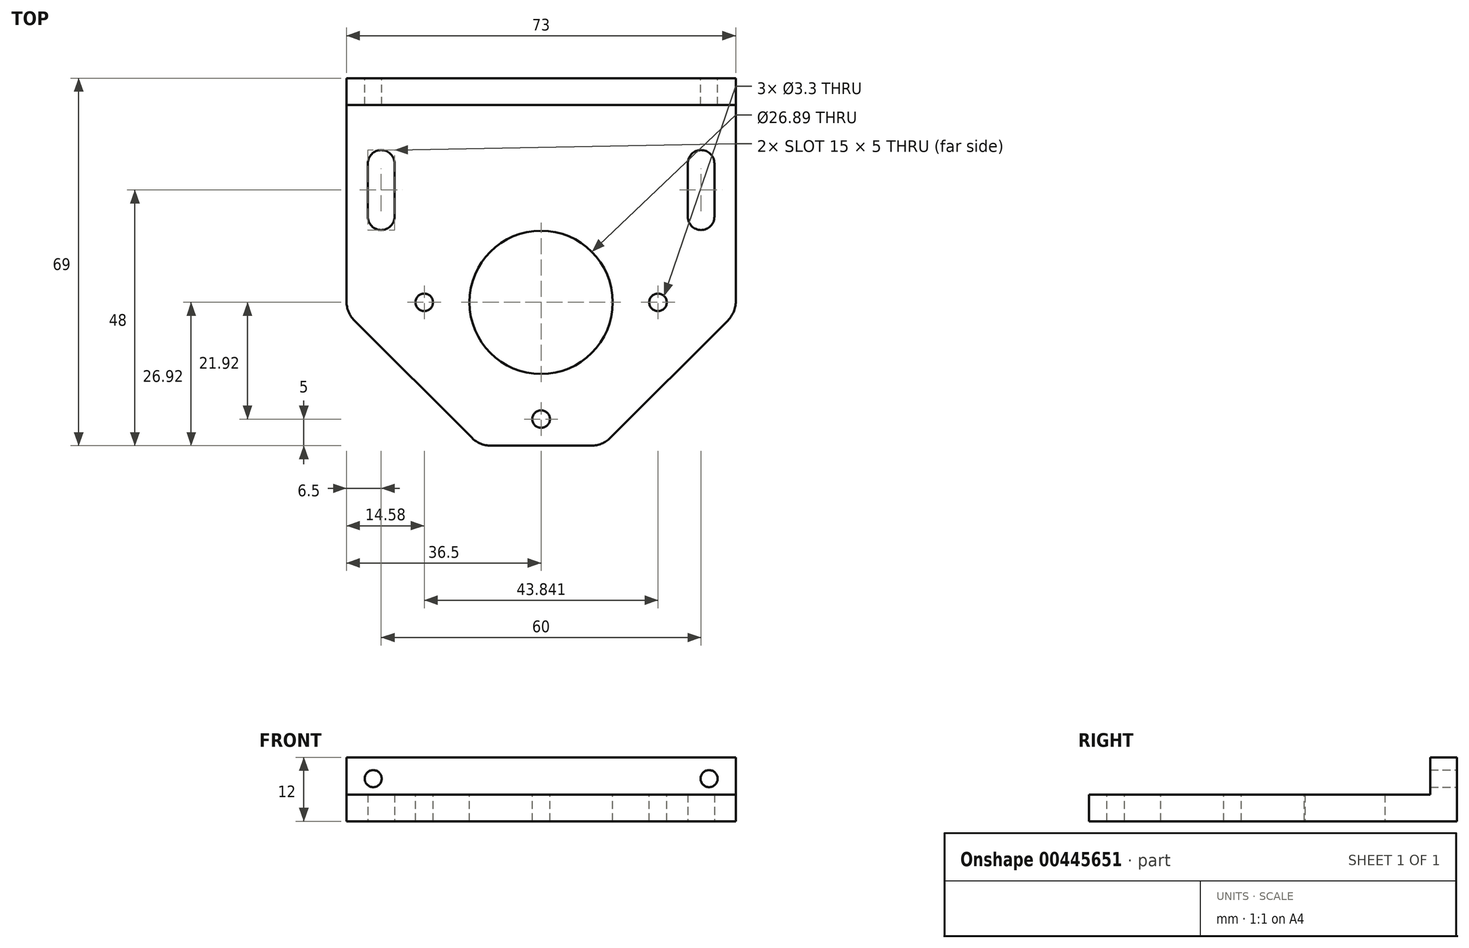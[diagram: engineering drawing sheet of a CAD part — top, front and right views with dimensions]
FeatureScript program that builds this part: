
annotation { "Feature Type Name" : "Feature", "Feature Type Description" : "" }
export const myFeature = defineFeature(function(context is Context, id is Id, definition is map)
    precondition{}
    {
        {
            var Q0;
            Q0=qCreatedBy(makeId("Top.planeOp"),FACE);
            var sketch = newSketch(context, id + "F0", { "sketchPlane" : qUnion([Q0])});
            skLineSegment(sketch, "E0.bottom", {"start": v(-36.5, -29.5) * mm, "end": v(36.5, -29.5) * mm});
            skLineSegment(sketch, "E0.top", {"start": v(-36.5, 29.5) * mm, "end": v(36.5, 29.5) * mm});
            skLineSegment(sketch, "E0.left", {"start": v(-36.5, -29.5) * mm, "end": v(-36.5, 29.5) * mm});
            skLineSegment(sketch, "E0.right", {"start": v(36.5, -29.5) * mm, "end": v(36.5, 29.5) * mm});
            skPoint(sketch, "E0.middle", {"position": v(0, 0) * mm});
            skLineSegment(sketch, "E1", {"start": v(-30, 23.5) * mm, "end": v(-30, 13.5) * mm});
            skLineSegment(sketch, "E2.1.0.0", {"start": v(30, 23.5) * mm, "end": v(30, 13.5) * mm});
            skLineSegment(sketch, "E2.direction1", {"start": v(-30, 13.5) * mm, "end": v(30, 13.5) * mm, "construction": true});
            skArc(sketch, "E3.0.startCap", {"start": v(-32.5, 23.5) * mm, "mid": v(-30, 26) * mm, "end": v(-27.5, 23.5) * mm});
            skArc(sketch, "E3.0.endCap", {"start": v(-27.5, 13.5) * mm, "mid": v(-30, 11) * mm, "end": v(-32.5, 13.5) * mm});
            skLineSegment(sketch, "E3.0.left", {"start": v(-27.5, 23.5) * mm, "end": v(-27.5, 13.5) * mm});
            skLineSegment(sketch, "E3.0.right", {"start": v(-32.5, 23.5) * mm, "end": v(-32.5, 13.5) * mm});
            skArc(sketch, "E3.1.startCap", {"start": v(27.5, 23.5) * mm, "mid": v(30, 26) * mm, "end": v(32.5, 23.5) * mm});
            skArc(sketch, "E3.1.endCap", {"start": v(32.5, 13.5) * mm, "mid": v(30, 11) * mm, "end": v(27.5, 13.5) * mm});
            skLineSegment(sketch, "E3.1.left", {"start": v(32.5, 23.5) * mm, "end": v(32.5, 13.5) * mm});
            skLineSegment(sketch, "E3.1.right", {"start": v(27.5, 23.5) * mm, "end": v(27.5, 13.5) * mm});
            skSolve(sketch);
        }
        {
            var Q0;
            Q0=qSketchRegion(id+"F0",true);
            extrude(context, id + "F1", {"entities" : qUnion([Q0]), "depth" : 5 * mm});
        }
        {
            var Q0;
            Q0=makeQuery(id+"F1.opExtrude","SWEPT_EDGE",EDGE,{"disambiguationData":[OSD([sQuery(id+"F0.wireOp",EDGE,"E0.bottom"),sQuery(id+"F0.wireOp",EDGE,"E0.left")])]});
            var Q1;
            Q1=makeQuery(id+"F1.opExtrude","SWEPT_EDGE",EDGE,{"disambiguationData":[OSD([sQuery(id+"F0.wireOp",EDGE,"E0.bottom"),sQuery(id+"F0.wireOp",EDGE,"E0.right")])]});
            chamfer(context, id + "F2", {"entities" : qUnion([Q0, Q1]), "width" : 25 * mm, "tangentPropagation" : true});
        }
        {
            var Q0;
            Q0=makeQuery(id+"F1.opExtrude","CAP_FACE",FACE,{"disambiguationData":[OSD([sQuery(id+"F0.wireOp",EDGE,"E0.bottom"),sQuery(id+"F0.wireOp",EDGE,"E0.top"),sQuery(id+"F0.wireOp",EDGE,"E0.left"),sQuery(id+"F0.wireOp",EDGE,"E0.right"),sQuery(id+"F0.wireOp",EDGE,"E3.0.startCap"),sQuery(id+"F0.wireOp",EDGE,"E3.0.endCap"),sQuery(id+"F0.wireOp",EDGE,"E3.0.left"),sQuery(id+"F0.wireOp",EDGE,"E3.0.right"),sQuery(id+"F0.wireOp",EDGE,"E3.1.startCap"),sQuery(id+"F0.wireOp",EDGE,"E3.1.endCap"),sQuery(id+"F0.wireOp",EDGE,"E3.1.left"),sQuery(id+"F0.wireOp",EDGE,"E3.1.right")])],"isStart":false});
            var sketch = newSketch(context, id + "F3", { "sketchPlane" : qUnion([Q0])});
            skPoint(sketch, "E4", {"position": v(0, -24.5) * mm});
            skLineSegment(sketch, "E5", {"start": v(0, -24.5) * mm, "end": v(-21.92, -2.58) * mm, "construction": true});
            skLineSegment(sketch, "E6", {"start": v(0, -24.5) * mm, "end": v(-61.13, -24.5) * mm, "construction": true});
            skLineSegment(sketch, "E7.MirrorCS", {"start": v(0, -24.5) * mm, "end": v(21.92, -2.58) * mm, "construction": true});
            skPoint(sketch, "E8", {"position": v(-21.92, -2.58) * mm});
            skPoint(sketch, "E9", {"position": v(21.92, -2.58) * mm});
            skCircle(sketch, "E10", {"center": v(0, -2.58) * mm, "radius": 13.45 * mm});
            skSolve(sketch);
        }
        {
            var Q0;
            Q0=sQuery(id+"F3.wireOp",VERTEX,"E8");
            var Q1;
            Q1=sQuery(id+"F3.wireOp",VERTEX,"E4");
            var Q2;
            Q2=sQuery(id+"F3.wireOp",VERTEX,"E9");
            var Q3;
            Q3=makeQuery(id+"F1.opExtrude","SWEPT_BODY",BODY,{"disambiguationData":[OSD([sQuery(id+"F0.wireOp",EDGE,"E0.bottom"),sQuery(id+"F0.wireOp",EDGE,"E0.top"),sQuery(id+"F0.wireOp",EDGE,"E0.left"),sQuery(id+"F0.wireOp",EDGE,"E0.right"),sQuery(id+"F0.wireOp",EDGE,"E3.0.startCap"),sQuery(id+"F0.wireOp",EDGE,"E3.0.endCap"),sQuery(id+"F0.wireOp",EDGE,"E3.0.left"),sQuery(id+"F0.wireOp",EDGE,"E3.0.right"),sQuery(id+"F0.wireOp",EDGE,"E3.1.startCap"),sQuery(id+"F0.wireOp",EDGE,"E3.1.endCap"),sQuery(id+"F0.wireOp",EDGE,"E3.1.left"),sQuery(id+"F0.wireOp",EDGE,"E3.1.right")])]});
            hole(context, id + "F4", {"style" : HoleStyle.SIMPLE, "endStyle" : HoleEndStyle.BLIND, "standardTappedOrClearance" : lookupTablePath({ "standard" : "ISO", "fit" : "Normal", "size" : "M3", "type" : "Clearance" }), "standardBlindInLast" : lookupTablePath({ "fit" : "Standard", "standard" : "ISO", "size" : "M3", "type" : "Clearance" }), "holeDiameter" : 3.3 * mm, "holeDepth" : 13.8 * mm, "tappedDepth" : 12 * mm, "tapClearance" : 3, "locations" : qUnion([Q0, Q1, Q2]), "scope" : qUnion([Q3])});
        }
        {
            var Q0;
            Q0=qSketchRegion(id+"F3",true);
            extrude(context, id + "F5", {"entities" : qUnion([Q0]), "operationType" : NewBodyOperationType.REMOVE, "endBound" : BoundingType.UP_TO_NEXT, "oppositeDirection" : true, "depth" : 25 * mm});
        }
        {
            var Q0;
            Q0=makeQuery(id+"F1.opExtrude","SWEPT_FACE",FACE,{"disambiguationData":[OSD([sQuery(id+"F0.wireOp",EDGE,"E0.top")])]});
            var sketch = newSketch(context, id + "F6", { "sketchPlane" : qUnion([Q0])});
            skLineSegment(sketch, "E11.bottom", {"start": v(-36.5, 5) * mm, "end": v(36.5, 5) * mm});
            skLineSegment(sketch, "E11.top", {"start": v(-36.5, 0) * mm, "end": v(36.5, 0) * mm});
            skLineSegment(sketch, "E11.left", {"start": v(-36.5, 5) * mm, "end": v(-36.5, 0) * mm});
            skLineSegment(sketch, "E11.right", {"start": v(36.5, 5) * mm, "end": v(36.5, 0) * mm});
            skSolve(sketch);
        }
        {
            var Q0;
            Q0=qSketchRegion(id+"F6",true);
            extrude(context, id + "F7", {"entities" : qUnion([Q0]), "operationType" : NewBodyOperationType.ADD, "depth" : 5 * mm});
        }
        {
            var Q0;
            Q0=makeQuery(id+"F7.opExtrude","CAP_FACE",FACE,{"disambiguationData":[OSD([sQuery(id+"F6.wireOp",EDGE,"E11.bottom"),sQuery(id+"F6.wireOp",EDGE,"E11.top"),sQuery(id+"F6.wireOp",EDGE,"E11.left"),sQuery(id+"F6.wireOp",EDGE,"E11.right")])],"isStart":false});
            var sketch = newSketch(context, id + "F8", { "sketchPlane" : qUnion([Q0])});
            skLineSegment(sketch, "E12.bottom", {"start": v(-36.5, 0) * mm, "end": v(36.5, 0) * mm});
            skLineSegment(sketch, "E12.top", {"start": v(-36.5, 12) * mm, "end": v(36.5, 12) * mm});
            skLineSegment(sketch, "E12.left", {"start": v(-36.5, 0) * mm, "end": v(-36.5, 12) * mm});
            skLineSegment(sketch, "E12.right", {"start": v(36.5, 0) * mm, "end": v(36.5, 12) * mm});
            skSolve(sketch);
        }
        {
            var Q0;
            Q0=qSketchRegion(id+"F8",true);
            extrude(context, id + "F9", {"entities" : qUnion([Q0]), "operationType" : NewBodyOperationType.ADD, "depth" : 5 * mm});
        }
        {
            var Q0;
            Q0=makeQuery(id+"F9.opExtrude","CAP_FACE",FACE,{"disambiguationData":[OSD([sQuery(id+"F8.wireOp",EDGE,"E12.bottom"),sQuery(id+"F8.wireOp",EDGE,"E12.top"),sQuery(id+"F8.wireOp",EDGE,"E12.left"),sQuery(id+"F8.wireOp",EDGE,"E12.right")])],"isStart":false});
            var sketch = newSketch(context, id + "F10", { "sketchPlane" : qUnion([Q0])});
            skPoint(sketch, "E13", {"position": v(-31.5, 8) * mm});
            skPoint(sketch, "E14.MirrorP", {"position": v(31.5, 8) * mm});
            skSolve(sketch);
        }
        {
            var Q0;
            Q0=sQuery(id+"F10.wireOp",VERTEX,"E13");
            var Q1;
            Q1=sQuery(id+"F10.wireOp",VERTEX,"E14.MirrorP");
            var Q2;
            Q2=makeQuery(id+"F1.opExtrude","SWEPT_BODY",BODY,{"disambiguationData":[OSD([sQuery(id+"F0.wireOp",EDGE,"E0.bottom"),sQuery(id+"F0.wireOp",EDGE,"E0.top"),sQuery(id+"F0.wireOp",EDGE,"E0.left"),sQuery(id+"F0.wireOp",EDGE,"E0.right"),sQuery(id+"F0.wireOp",EDGE,"E3.0.startCap"),sQuery(id+"F0.wireOp",EDGE,"E3.0.endCap"),sQuery(id+"F0.wireOp",EDGE,"E3.0.left"),sQuery(id+"F0.wireOp",EDGE,"E3.0.right"),sQuery(id+"F0.wireOp",EDGE,"E3.1.startCap"),sQuery(id+"F0.wireOp",EDGE,"E3.1.endCap"),sQuery(id+"F0.wireOp",EDGE,"E3.1.left"),sQuery(id+"F0.wireOp",EDGE,"E3.1.right")])]});
            hole(context, id + "F11", {"style" : HoleStyle.SIMPLE, "endStyle" : HoleEndStyle.THROUGH, "standardTappedOrClearance" : lookupTablePath({ "standard" : "ISO", "engagement" : "75%", "pitch" : "0.75 mm", "size" : "M4", "type" : "Tapped" }), "standardBlindInLast" : lookupTablePath({ "standard" : "ISO", "engagement" : "75%", "pitch" : "0.75 mm", "size" : "M4", "type" : "Tapped" }), "holeDiameter" : 3.2 * mm, "showTappedDepth" : true, "isTappedThrough" : true, "tappedDepth" : 12 * mm, "tapClearance" : 3, "locations" : qUnion([Q0, Q1]), "scope" : qUnion([Q2])});
        }
        {
            var Q0;
            {var subQ0=sQuery(id+"F0.wireOp",EDGE,"E0.right");Q0=makeQuery(id+"F2.opChamfer","BLEND_EDGE",EDGE,{"blendedFrom":[makeQuery(id+"F1.opExtrude","SWEPT_EDGE",EDGE,{"disambiguationData":[OSD([sQuery(id+"F0.wireOp",EDGE,"E0.bottom"),subQ0])]}),makeQuery(id+"F1.opExtrude","SWEPT_FACE",FACE,{"disambiguationData":[OSD([subQ0])]})],"blendedInto":[makeQuery(id+"F1.opExtrude","SWEPT_FACE",FACE,{"disambiguationData":[OSD([subQ0])]})]});}
            var Q1;
            {var subQ0=sQuery(id+"F0.wireOp",EDGE,"E0.bottom");Q1=makeQuery(id+"F2.opChamfer","BLEND_EDGE",EDGE,{"blendedFrom":[makeQuery(id+"F1.opExtrude","SWEPT_EDGE",EDGE,{"disambiguationData":[OSD([subQ0,sQuery(id+"F0.wireOp",EDGE,"E0.right")])]}),makeQuery(id+"F1.opExtrude","SWEPT_FACE",FACE,{"disambiguationData":[OSD([subQ0])]})],"blendedInto":[makeQuery(id+"F1.opExtrude","SWEPT_FACE",FACE,{"disambiguationData":[OSD([subQ0])]})]});}
            var Q2;
            {var subQ0=sQuery(id+"F0.wireOp",EDGE,"E0.bottom");Q2=makeQuery(id+"F2.opChamfer","BLEND_EDGE",EDGE,{"blendedFrom":[makeQuery(id+"F1.opExtrude","SWEPT_EDGE",EDGE,{"disambiguationData":[OSD([subQ0,sQuery(id+"F0.wireOp",EDGE,"E0.left")])]}),makeQuery(id+"F1.opExtrude","SWEPT_FACE",FACE,{"disambiguationData":[OSD([subQ0])]})],"blendedInto":[makeQuery(id+"F1.opExtrude","SWEPT_FACE",FACE,{"disambiguationData":[OSD([subQ0])]})]});}
            var Q3;
            {var subQ0=sQuery(id+"F0.wireOp",EDGE,"E0.left");Q3=makeQuery(id+"F2.opChamfer","BLEND_EDGE",EDGE,{"blendedFrom":[makeQuery(id+"F1.opExtrude","SWEPT_EDGE",EDGE,{"disambiguationData":[OSD([sQuery(id+"F0.wireOp",EDGE,"E0.bottom"),subQ0])]}),makeQuery(id+"F1.opExtrude","SWEPT_FACE",FACE,{"disambiguationData":[OSD([subQ0])]})],"blendedInto":[makeQuery(id+"F1.opExtrude","SWEPT_FACE",FACE,{"disambiguationData":[OSD([subQ0])]})]});}
            fillet(context, id + "F12", {"entities" : qUnion([Q0, Q1, Q2, Q3]), "radius" : 5 * mm, "tangentPropagation" : true, "allowEdgeOverflow" : false});
        }
    });
